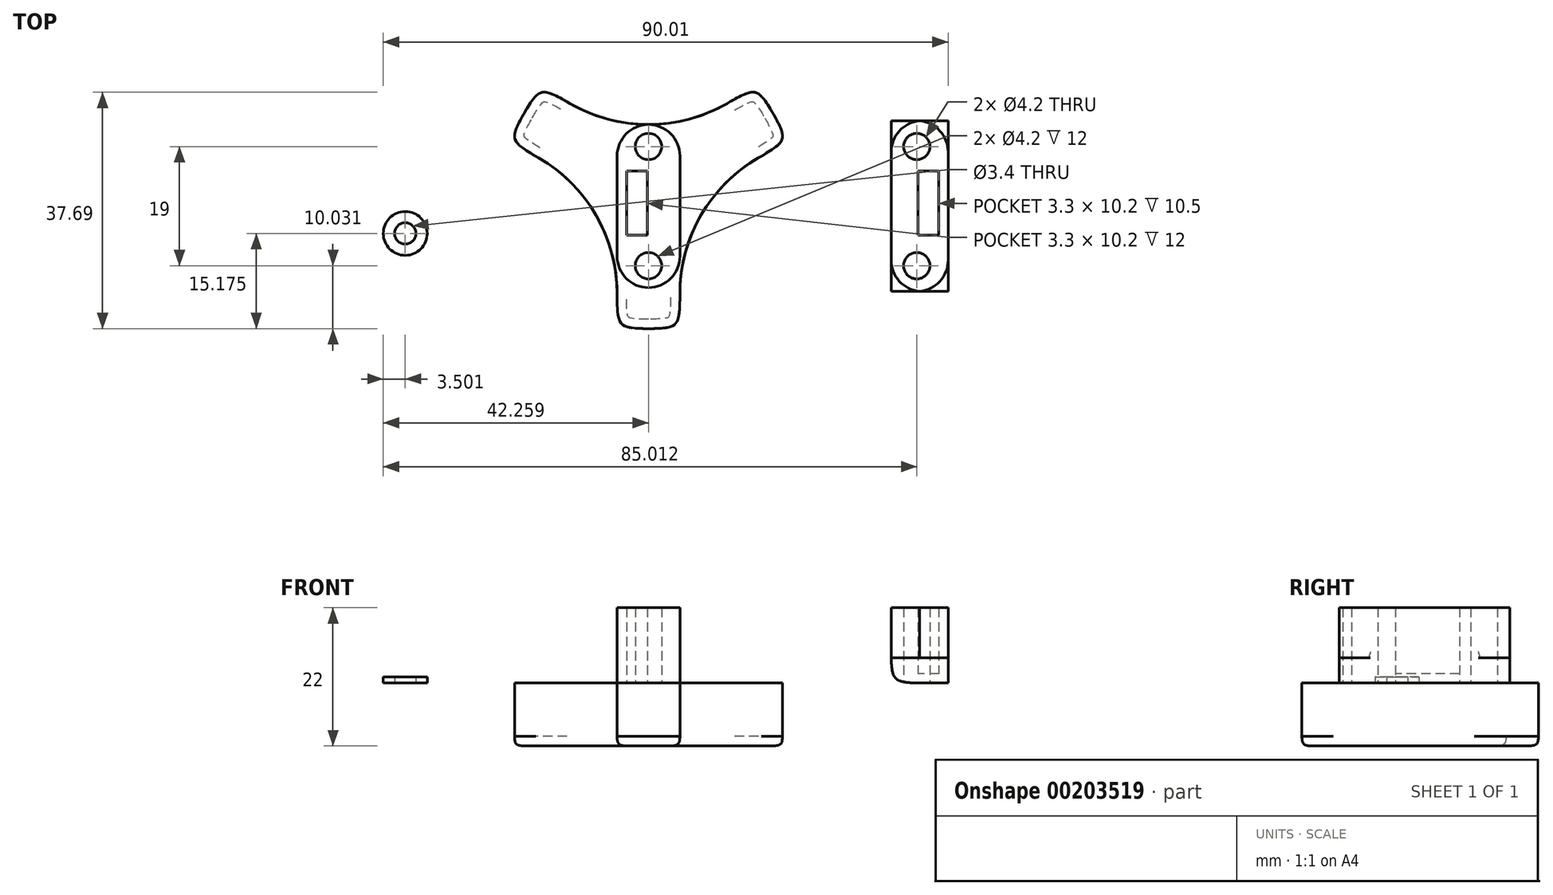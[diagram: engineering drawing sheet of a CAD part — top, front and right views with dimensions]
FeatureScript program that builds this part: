
annotation { "Feature Type Name" : "Feature", "Feature Type Description" : "" }
export const myFeature = defineFeature(function(context is Context, id is Id, definition is map)
    precondition{}
    {
        {
            var Q0;
            Q0=qCreatedBy(makeId("Top.planeOp"),FACE);
            var sketch = newSketch(context, id + "F0", { "sketchPlane" : qUnion([Q0])});
            skLineSegment(sketch, "E0.bottom", {"start": v(-1.4, -6.47) * mm, "end": v(8.6, -6.47) * mm});
            skLineSegment(sketch, "E0.top", {"start": v(-1.4, -26.47) * mm, "end": v(8.6, -26.47) * mm});
            skLineSegment(sketch, "E0.left", {"start": v(-1.4, -6.47) * mm, "end": v(-1.4, -26.47) * mm});
            skLineSegment(sketch, "E0.right", {"start": v(8.6, -6.47) * mm, "end": v(8.6, -26.47) * mm});
            skLineSegment(sketch, "E1", {"start": v(3.6, -26.47) * mm, "end": v(3.6, 13.87) * mm, "construction": true});
            skPoint(sketch, "E2", {"position": v(3.6, -3.58) * mm});
            skLineSegment(sketch, "E3", {"start": v(-1.4, -6.47) * mm, "end": v(3.6, -3.58) * mm});
            skLineSegment(sketch, "E4", {"start": v(8.6, -6.47) * mm, "end": v(3.6, -3.58) * mm});
            skLineSegment(sketch, "E5.1.0", {"start": v(3.6, 2.2) * mm, "end": v(3.6, -3.58) * mm});
            skLineSegment(sketch, "E5.1.1", {"start": v(8.6, -6.47) * mm, "end": v(25.92, 3.53) * mm});
            skLineSegment(sketch, "E5.1.4", {"start": v(8.6, -6.47) * mm, "end": v(3.6, 2.2) * mm});
            skLineSegment(sketch, "E5.1.5", {"start": v(25.92, 3.53) * mm, "end": v(20.92, 12.2) * mm});
            skLineSegment(sketch, "E5.1.6", {"start": v(3.6, 2.2) * mm, "end": v(20.92, 12.2) * mm});
            skLineSegment(sketch, "E5.2.1", {"start": v(3.6, 2.2) * mm, "end": v(-13.72, 12.2) * mm});
            skLineSegment(sketch, "E5.2.2", {"start": v(3.6, 2.2) * mm, "end": v(3.6, -3.58) * mm});
            skLineSegment(sketch, "E5.2.4", {"start": v(3.6, 2.2) * mm, "end": v(-1.4, -6.47) * mm});
            skLineSegment(sketch, "E5.2.5", {"start": v(-13.72, 12.2) * mm, "end": v(-18.72, 3.53) * mm});
            skLineSegment(sketch, "E5.2.6", {"start": v(-1.4, -6.47) * mm, "end": v(-18.72, 3.53) * mm});
            skPoint(sketch, "E6", {"position": v(3.6, -7.8) * mm});
            skSolve(sketch);
        }
        {
            var Q0;
            Q0=qSketchRegion(id+"F0",true);
            extrude(context, id + "F1", {"entities" : qUnion([Q0]), "oppositeDirection" : true, "depth" : 10 * mm});
        }
        {
            var Q0;
            Q0=makeQuery(id+"F1.opExtrude","SWEPT_EDGE",EDGE,{"disambiguationData":[OSD([sQuery(id+"F0.wireOp",EDGE,"E5.2.1"),sQuery(id+"F0.wireOp",EDGE,"E5.2.5")])]});
            var Q1;
            Q1=makeQuery(id+"F1.opExtrude","SWEPT_EDGE",EDGE,{"disambiguationData":[OSD([sQuery(id+"F0.wireOp",EDGE,"E5.2.5"),sQuery(id+"F0.wireOp",EDGE,"E5.2.6")])]});
            var Q2;
            Q2=makeQuery(id+"F1.opExtrude","SWEPT_EDGE",EDGE,{"disambiguationData":[OSD([sQuery(id+"F0.wireOp",EDGE,"E5.1.5"),sQuery(id+"F0.wireOp",EDGE,"E5.1.6")])]});
            var Q3;
            Q3=makeQuery(id+"F1.opExtrude","SWEPT_EDGE",EDGE,{"disambiguationData":[OSD([sQuery(id+"F0.wireOp",EDGE,"E5.1.1"),sQuery(id+"F0.wireOp",EDGE,"E5.1.5")])]});
            var Q4;
            Q4=makeQuery(id+"F1.opExtrude","SWEPT_EDGE",EDGE,{"disambiguationData":[OSD([sQuery(id+"F0.wireOp",EDGE,"E0.top"),sQuery(id+"F0.wireOp",EDGE,"E0.right")])]});
            var Q5;
            Q5=makeQuery(id+"F1.opExtrude","SWEPT_EDGE",EDGE,{"disambiguationData":[OSD([sQuery(id+"F0.wireOp",EDGE,"E0.top"),sQuery(id+"F0.wireOp",EDGE,"E0.left")])]});
            fillet(context, id + "F2", {"entities" : qUnion([Q0, Q1, Q2, Q3, Q4, Q5]), "radius" : 5 * mm, "tangentPropagation" : true, "rho" : 0.7, "crossSection" : FilletCrossSection.CONIC, "allowEdgeOverflow" : false});
        }
        {
            var Q0;
            Q0=makeQuery(id+"F1.opExtrude","SWEPT_EDGE",EDGE,{"disambiguationData":[OSD([sQuery(id+"F0.wireOp",EDGE,"E0.bottom"),sQuery(id+"F0.wireOp",EDGE,"E0.right"),sQuery(id+"F0.wireOp",EDGE,"E5.1.1"),sQuery(id+"F0.wireOp",EDGE,"E4"),sQuery(id+"F0.wireOp",EDGE,"E5.1.4")])]});
            var Q1;
            Q1=makeQuery(id+"F1.opExtrude","SWEPT_EDGE",EDGE,{"disambiguationData":[OSD([sQuery(id+"F0.wireOp",EDGE,"E0.bottom"),sQuery(id+"F0.wireOp",EDGE,"E0.left"),sQuery(id+"F0.wireOp",EDGE,"E3"),sQuery(id+"F0.wireOp",EDGE,"E5.2.4"),sQuery(id+"F0.wireOp",EDGE,"E5.2.6")])]});
            var Q2;
            Q2=makeQuery(id+"F1.opExtrude","SWEPT_EDGE",EDGE,{"disambiguationData":[OSD([sQuery(id+"F0.wireOp",EDGE,"E5.1.4"),sQuery(id+"F0.wireOp",EDGE,"E5.1.6"),sQuery(id+"F0.wireOp",EDGE,"E5.2.1"),sQuery(id+"F0.wireOp",EDGE,"E5.2.2"),sQuery(id+"F0.wireOp",EDGE,"E5.2.4")])]});
            fillet(context, id + "F3", {"entities" : qUnion([Q0, Q1, Q2]), "radius" : 25 * mm, "allowEdgeOverflow" : false});
        }
        {
            var Q0;
            Q0=qCreatedBy(makeId("Top.planeOp"),FACE);
            var sketch = newSketch(context, id + "F4", { "sketchPlane" : qUnion([Q0])});
            skLineSegment(sketch, "E7.bottom", {"start": v(-1.4, 6.06) * mm, "end": v(8.6, 6.06) * mm});
            skLineSegment(sketch, "E7.top", {"start": v(-1.4, -19.94) * mm, "end": v(8.6, -19.94) * mm});
            skLineSegment(sketch, "E7.left", {"start": v(-1.4, 6.06) * mm, "end": v(-1.4, -19.94) * mm});
            skLineSegment(sketch, "E7.right", {"start": v(8.6, 6.06) * mm, "end": v(8.6, -19.94) * mm});
            skLineSegment(sketch, "E8", {"start": v(3.6, 6.06) * mm, "end": v(3.6, -19.94) * mm, "construction": true});
            skLineSegment(sketch, "E9.bottom", {"start": v(0.1, -1.37) * mm, "end": v(3.4, -1.37) * mm});
            skLineSegment(sketch, "E9.top", {"start": v(0.1, -11.57) * mm, "end": v(3.4, -11.57) * mm});
            skLineSegment(sketch, "E9.left", {"start": v(0.1, -1.37) * mm, "end": v(0.1, -11.57) * mm});
            skLineSegment(sketch, "E9.right", {"start": v(3.4, -1.37) * mm, "end": v(3.4, -11.57) * mm});
            skCircle(sketch, "E10", {"center": v(3.6, 2.56) * mm, "radius": 2.1 * mm});
            skCircle(sketch, "E11", {"center": v(3.6, -16.44) * mm, "radius": 2.1 * mm});
            skLineSegment(sketch, "E12", {"start": v(-1.4, -6.94) * mm, "end": v(8.6, -6.94) * mm, "construction": true});
            skPoint(sketch, "E13", {"position": v(0.1, -6.47) * mm});
            skLineSegment(sketch, "E14", {"start": v(24.98, 11.89) * mm, "end": v(24.98, -28.7) * mm, "construction": true});
            skLineSegment(sketch, "E15.MirrorCS", {"start": v(51.35, 6.06) * mm, "end": v(51.35, -19.94) * mm});
            skCircle(sketch, "E16.MirrorC", {"center": v(46.35, 2.56) * mm, "radius": 2.1 * mm});
            skLineSegment(sketch, "E17.MirrorCS", {"start": v(49.85, -1.37) * mm, "end": v(49.85, -11.57) * mm});
            skLineSegment(sketch, "E18.MirrorCS", {"start": v(49.85, -1.37) * mm, "end": v(46.55, -1.37) * mm});
            skLineSegment(sketch, "E19.MirrorCS", {"start": v(46.55, -1.37) * mm, "end": v(46.55, -11.57) * mm});
            skLineSegment(sketch, "E20.MirrorCS", {"start": v(49.85, -11.57) * mm, "end": v(46.55, -11.57) * mm});
            skCircle(sketch, "E21.MirrorC", {"center": v(46.35, -16.44) * mm, "radius": 2.1 * mm});
            skLineSegment(sketch, "E22", {"start": v(51.35, 6.06) * mm, "end": v(51.35, 6.66) * mm});
            skLineSegment(sketch, "E23", {"start": v(51.35, 6.66) * mm, "end": v(42.25, 6.66) * mm});
            skLineSegment(sketch, "E24", {"start": v(42.25, 6.66) * mm, "end": v(42.25, -20.54) * mm});
            skLineSegment(sketch, "E25", {"start": v(42.25, -20.54) * mm, "end": v(51.35, -20.54) * mm});
            skLineSegment(sketch, "E26", {"start": v(51.35, -20.54) * mm, "end": v(51.35, -19.94) * mm});
            skSolve(sketch);
        }
        {
            var Q0;
            Q0=makeQuery(id+"F4.imprint","IMPRINT",FACE,{"disambiguationData":[TD([[makeQuery(id+"F4.imprint","IMPRINT",EDGE,{"derivedFrom":sQuery(id+"F4.wireOp",EDGE,"E7.bottom")}),-1.0]])]});
            extrude(context, id + "F5", {"entities" : qUnion([Q0]), "operationType" : NewBodyOperationType.ADD, "depth" : 12 * mm});
        }
        {
            var Q0;
            Q0=makeQuery(id+"F4.imprint","IMPRINT",FACE,{"disambiguationData":[TD([[makeQuery(id+"F4.imprint","IMPRINT",EDGE,{"derivedFrom":sQuery(id+"F4.wireOp",EDGE,"E15.MirrorCS")}),-1.0]])]});
            extrude(context, id + "F6", {"entities" : qUnion([Q0]), "depth" : 12 * mm});
        }
        {
            var Q0;
            Q0=makeQuery(id+"F4.imprint","IMPRINT",FACE,{"disambiguationData":[TD([[makeQuery(id+"F4.imprint","IMPRINT",EDGE,{"derivedFrom":sQuery(id+"F4.wireOp",EDGE,"E15.MirrorCS")}),-1.0]])]});
            var Q1;
            Q1=makeQuery(id+"F4.imprint","IMPRINT",FACE,{"disambiguationData":[TD([[makeQuery(id+"F4.imprint","IMPRINT",EDGE,{"derivedFrom":sQuery(id+"F4.wireOp",EDGE,"E16.MirrorC")}),-1.0]])]});
            var Q2;
            Q2=makeQuery(id+"F4.imprint","IMPRINT",FACE,{"disambiguationData":[TD([[makeQuery(id+"F4.imprint","IMPRINT",EDGE,{"derivedFrom":sQuery(id+"F4.wireOp",EDGE,"E17.MirrorCS")}),-1.0]])]});
            var Q3;
            Q3=makeQuery(id+"F4.imprint","IMPRINT",FACE,{"disambiguationData":[TD([[makeQuery(id+"F4.imprint","IMPRINT",EDGE,{"derivedFrom":sQuery(id+"F4.wireOp",EDGE,"E21.MirrorC")}),-1.0]])]});
            extrude(context, id + "F7", {"entities" : qUnion([Q0, Q1, Q2, Q3]), "operationType" : NewBodyOperationType.ADD, "depth" : 1.5 * mm});
        }
        {
            var Q0;
            Q0=qCreatedBy(makeId("Top.planeOp"),FACE);
            var sketch = newSketch(context, id + "F8", { "sketchPlane" : qUnion([Q0])});
            skCircle(sketch, "E27", {"center": v(-35.16, -11.3) * mm, "radius": 3.5 * mm});
            skCircle(sketch, "E28", {"center": v(-35.16, -11.3) * mm, "radius": 1.7 * mm});
            skLineSegment(sketch, "E29", {"start": v(-46.83, -11.3) * mm, "end": v(-19.95, -11.3) * mm, "construction": true});
            skPoint(sketch, "E30", {"position": v(-38.66, -11.3) * mm});
            skPoint(sketch, "E31", {"position": v(-31.66, -11.3) * mm});
            skSolve(sketch);
        }
        {
            var Q0;
            Q0=makeQuery(id+"F8.imprint","IMPRINT",FACE,{"disambiguationData":[TD([[makeQuery(id+"F8.imprint","IMPRINT",EDGE,{"derivedFrom":sQuery(id+"F8.wireOp",EDGE,"E27")}),1.0]])]});
            extrude(context, id + "F9", {"entities" : qUnion([Q0]), "depth" : 1 * mm});
        }
        {
            var Q0;
            Q0=makeQuery(id+"F5.opExtrude","SWEPT_EDGE",EDGE,{"disambiguationData":[OSD([sQuery(id+"F4.wireOp",EDGE,"E7.top"),sQuery(id+"F4.wireOp",EDGE,"E7.left")])]});
            var Q1;
            Q1=makeQuery(id+"F5.opExtrude","SWEPT_EDGE",EDGE,{"disambiguationData":[OSD([sQuery(id+"F4.wireOp",EDGE,"E7.top"),sQuery(id+"F4.wireOp",EDGE,"E7.right")])]});
            var Q2;
            Q2=makeQuery(id+"F5.opExtrude","SWEPT_EDGE",EDGE,{"disambiguationData":[OSD([sQuery(id+"F4.wireOp",EDGE,"E7.bottom"),sQuery(id+"F4.wireOp",EDGE,"E7.left")])]});
            var Q3;
            Q3=makeQuery(id+"F5.opExtrude","SWEPT_EDGE",EDGE,{"disambiguationData":[OSD([sQuery(id+"F4.wireOp",EDGE,"E7.bottom"),sQuery(id+"F4.wireOp",EDGE,"E7.right")])]});
            var Q4;
            Q4=makeQuery(id+"F6.opExtrude","SWEPT_EDGE",EDGE,{"disambiguationData":[OSD([sQuery(id+"F4.wireOp",EDGE,"E24"),sQuery(id+"F4.wireOp",EDGE,"E25")])]});
            var Q5;
            Q5=makeQuery(id+"F6.opExtrude","SWEPT_EDGE",EDGE,{"disambiguationData":[OSD([sQuery(id+"F4.wireOp",EDGE,"E25"),sQuery(id+"F4.wireOp",EDGE,"E26")])]});
            var Q6;
            Q6=makeQuery(id+"F6.opExtrude","SWEPT_EDGE",EDGE,{"disambiguationData":[OSD([sQuery(id+"F4.wireOp",EDGE,"E23"),sQuery(id+"F4.wireOp",EDGE,"E24")])]});
            var Q7;
            Q7=makeQuery(id+"F6.opExtrude","SWEPT_EDGE",EDGE,{"disambiguationData":[OSD([sQuery(id+"F4.wireOp",EDGE,"E22"),sQuery(id+"F4.wireOp",EDGE,"E23")])]});
            fillet(context, id + "F10", {"entities" : qUnion([Q0, Q1, Q2, Q3, Q4, Q5, Q6, Q7]), "radius" : 5 * mm, "tangentPropagation" : true, "allowEdgeOverflow" : false});
        }
        {
            var Q0;
            Q0=makeQuery(id+"F4.imprint","IMPRINT",FACE,{"disambiguationData":[TD([[makeQuery(id+"F4.imprint","IMPRINT",EDGE,{"derivedFrom":sQuery(id+"F4.wireOp",EDGE,"E16.MirrorC")}),-1.0]])]});
            var Q1;
            Q1=makeQuery(id+"F4.imprint","IMPRINT",FACE,{"disambiguationData":[TD([[makeQuery(id+"F4.imprint","IMPRINT",EDGE,{"derivedFrom":sQuery(id+"F4.wireOp",EDGE,"E21.MirrorC")}),-1.0]])]});
            extrude(context, id + "F11", {"entities" : qUnion([Q0, Q1]), "operationType" : NewBodyOperationType.ADD, "depth" : 4 * mm});
        }
        {
            var Q0;
            Q0=makeQuery(id+"F6.opExtrude","CAP_EDGE",EDGE,{"disambiguationData":[OSD([sQuery(id+"F4.wireOp",EDGE,"E24")])],"isStart":true});
            var Q1;
            {var subQ0=sQuery(id+"F4.wireOp",EDGE,"E23");var subQ1=sQuery(id+"F4.wireOp",EDGE,"E24");var subQ2=sQuery(id+"F4.wireOp",EDGE,"E15.MirrorCS");var subQ3=sQuery(id+"F4.wireOp",EDGE,"E22");var subQ4=sQuery(id+"F4.wireOp",EDGE,"E25");var subQ5=sQuery(id+"F4.wireOp",EDGE,"E26");Q1=makeQuery(id+"F10.opFillet","BLEND_EDGE",EDGE,{"blendedFrom":[makeQuery(id+"F6.opExtrude","SWEPT_EDGE",EDGE,{"disambiguationData":[OSD([subQ0,subQ1])]}),makeQuery(id+"F7.boolean.opBoolean","MERGE",FACE,{"derivedFrom":[makeQuery(id+"F6.opExtrude","CAP_FACE",FACE,{"disambiguationData":[OSD([subQ2,sQuery(id+"F4.wireOp",EDGE,"E16.MirrorC"),sQuery(id+"F4.wireOp",EDGE,"E17.MirrorCS"),sQuery(id+"F4.wireOp",EDGE,"E18.MirrorCS"),sQuery(id+"F4.wireOp",EDGE,"E19.MirrorCS"),sQuery(id+"F4.wireOp",EDGE,"E20.MirrorCS"),sQuery(id+"F4.wireOp",EDGE,"E21.MirrorC"),subQ3,subQ0,subQ1,subQ4,subQ5])],"isStart":true}),makeQuery(id+"F7.opExtrude","CAP_FACE",FACE,{"disambiguationData":[OSD([subQ2,subQ3,subQ0,subQ1,subQ4,subQ5])],"isStart":true})]})],"blendedInto":[makeQuery(id+"F7.boolean.opBoolean","MERGE",FACE,{"derivedFrom":[makeQuery(id+"F6.opExtrude","CAP_FACE",FACE,{"disambiguationData":[OSD([subQ2,sQuery(id+"F4.wireOp",EDGE,"E16.MirrorC"),sQuery(id+"F4.wireOp",EDGE,"E17.MirrorCS"),sQuery(id+"F4.wireOp",EDGE,"E18.MirrorCS"),sQuery(id+"F4.wireOp",EDGE,"E19.MirrorCS"),sQuery(id+"F4.wireOp",EDGE,"E20.MirrorCS"),sQuery(id+"F4.wireOp",EDGE,"E21.MirrorC"),subQ3,subQ0,subQ1,subQ4,subQ5])],"isStart":true}),makeQuery(id+"F7.opExtrude","CAP_FACE",FACE,{"disambiguationData":[OSD([subQ2,subQ3,subQ0,subQ1,subQ4,subQ5])],"isStart":true})]})]});}
            var Q2;
            {var subQ0=sQuery(id+"F4.wireOp",EDGE,"E24");var subQ1=sQuery(id+"F4.wireOp",EDGE,"E25");var subQ2=sQuery(id+"F4.wireOp",EDGE,"E15.MirrorCS");var subQ3=sQuery(id+"F4.wireOp",EDGE,"E22");var subQ4=sQuery(id+"F4.wireOp",EDGE,"E23");var subQ5=sQuery(id+"F4.wireOp",EDGE,"E26");Q2=makeQuery(id+"F10.opFillet","BLEND_EDGE",EDGE,{"blendedFrom":[makeQuery(id+"F6.opExtrude","SWEPT_EDGE",EDGE,{"disambiguationData":[OSD([subQ0,subQ1])]}),makeQuery(id+"F7.boolean.opBoolean","MERGE",FACE,{"derivedFrom":[makeQuery(id+"F6.opExtrude","CAP_FACE",FACE,{"disambiguationData":[OSD([subQ2,sQuery(id+"F4.wireOp",EDGE,"E16.MirrorC"),sQuery(id+"F4.wireOp",EDGE,"E17.MirrorCS"),sQuery(id+"F4.wireOp",EDGE,"E18.MirrorCS"),sQuery(id+"F4.wireOp",EDGE,"E19.MirrorCS"),sQuery(id+"F4.wireOp",EDGE,"E20.MirrorCS"),sQuery(id+"F4.wireOp",EDGE,"E21.MirrorC"),subQ3,subQ4,subQ0,subQ1,subQ5])],"isStart":true}),makeQuery(id+"F7.opExtrude","CAP_FACE",FACE,{"disambiguationData":[OSD([subQ2,subQ3,subQ4,subQ0,subQ1,subQ5])],"isStart":true})]})],"blendedInto":[makeQuery(id+"F7.boolean.opBoolean","MERGE",FACE,{"derivedFrom":[makeQuery(id+"F6.opExtrude","CAP_FACE",FACE,{"disambiguationData":[OSD([subQ2,sQuery(id+"F4.wireOp",EDGE,"E16.MirrorC"),sQuery(id+"F4.wireOp",EDGE,"E17.MirrorCS"),sQuery(id+"F4.wireOp",EDGE,"E18.MirrorCS"),sQuery(id+"F4.wireOp",EDGE,"E19.MirrorCS"),sQuery(id+"F4.wireOp",EDGE,"E20.MirrorCS"),sQuery(id+"F4.wireOp",EDGE,"E21.MirrorC"),subQ3,subQ4,subQ0,subQ1,subQ5])],"isStart":true}),makeQuery(id+"F7.opExtrude","CAP_FACE",FACE,{"disambiguationData":[OSD([subQ2,subQ3,subQ4,subQ0,subQ1,subQ5])],"isStart":true})]})]});}
            fillet(context, id + "F12", {"entities" : qUnion([Q0, Q1, Q2]), "radius" : 5 * mm, "tangentPropagation" : true, "rho" : 0.7, "crossSection" : FilletCrossSection.CONIC, "allowEdgeOverflow" : false});
        }
        {
            var Q0;
            Q0=makeQuery(id+"F1.opExtrude","CAP_FACE",FACE,{"disambiguationData":[OSD([sQuery(id+"F0.wireOp",EDGE,"E0.top"),sQuery(id+"F0.wireOp",EDGE,"E0.left"),sQuery(id+"F0.wireOp",EDGE,"E0.right"),sQuery(id+"F0.wireOp",EDGE,"E5.1.1"),sQuery(id+"F0.wireOp",EDGE,"E5.1.5"),sQuery(id+"F0.wireOp",EDGE,"E5.1.6"),sQuery(id+"F0.wireOp",EDGE,"E5.2.1"),sQuery(id+"F0.wireOp",EDGE,"E5.2.5"),sQuery(id+"F0.wireOp",EDGE,"E5.2.6")])],"isStart":false});
            fillet(context, id + "F13", {"entities" : qUnion([Q0]), "radius" : 1.5 * mm, "tangentPropagation" : true, "rho" : 0.6, "crossSection" : FilletCrossSection.CONIC, "allowEdgeOverflow" : false});
        }
    });
